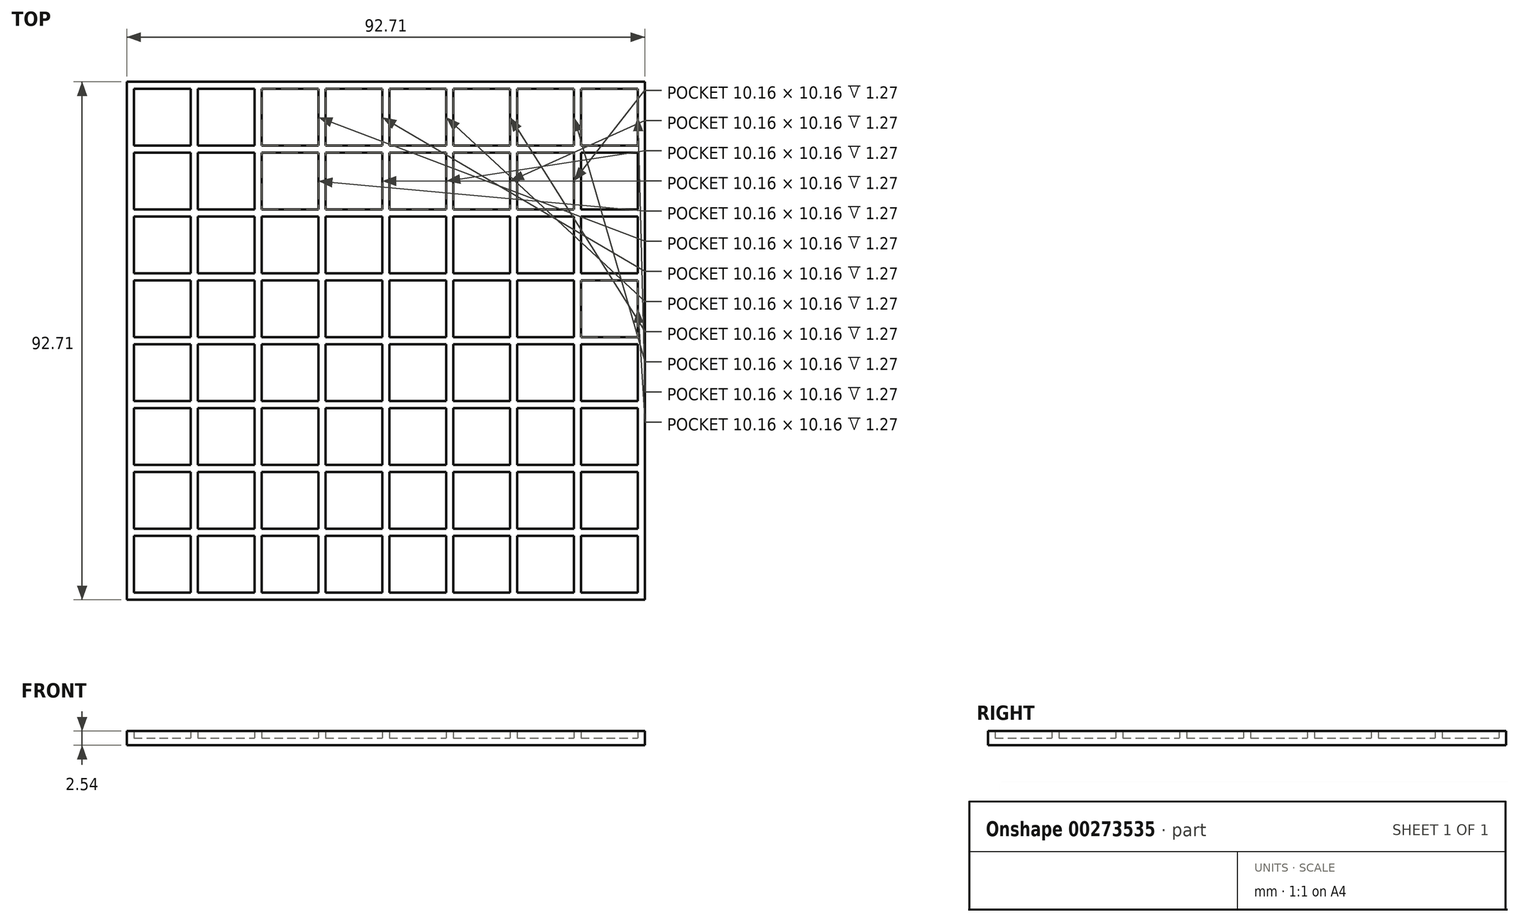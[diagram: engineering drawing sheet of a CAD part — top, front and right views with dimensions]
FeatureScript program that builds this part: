
annotation { "Feature Type Name" : "Feature", "Feature Type Description" : "" }
export const myFeature = defineFeature(function(context is Context, id is Id, definition is map)
    precondition{}
    {
        {
            var Q0;
            Q0=qCreatedBy(makeId("Top.planeOp"),FACE);
            var sketch = newSketch(context, id + "F0", { "sketchPlane" : qUnion([Q0])});
            skLineSegment(sketch, "E0.top", {"start": v(0, 92.7) * mm, "end": v(92.7, 92.7) * mm});
            skLineSegment(sketch, "E0.left", {"start": v(0, 0) * mm, "end": v(0, 92.7) * mm});
            skLineSegment(sketch, "E0.right", {"start": v(92.7, 0) * mm, "end": v(92.7, 92.7) * mm});
            skLineSegment(sketch, "E1.bottom", {"start": v(1.27, 1.27) * mm, "end": v(11.43, 1.27) * mm});
            skLineSegment(sketch, "E1.top", {"start": v(1.27, 11.43) * mm, "end": v(11.43, 11.43) * mm});
            skLineSegment(sketch, "E1.left", {"start": v(1.27, 1.27) * mm, "end": v(1.27, 11.43) * mm});
            skLineSegment(sketch, "E1.right", {"start": v(11.43, 1.27) * mm, "end": v(11.43, 11.43) * mm});
            skLineSegment(sketch, "E2.bottom", {"start": v(12.7, 1.27) * mm, "end": v(22.86, 1.27) * mm});
            skLineSegment(sketch, "E2.top", {"start": v(12.7, 11.43) * mm, "end": v(22.86, 11.43) * mm});
            skLineSegment(sketch, "E2.left", {"start": v(12.7, 1.27) * mm, "end": v(12.7, 11.43) * mm});
            skLineSegment(sketch, "E2.right", {"start": v(22.86, 1.27) * mm, "end": v(22.86, 11.43) * mm});
            skLineSegment(sketch, "E3.bottom", {"start": v(24.13, 1.27) * mm, "end": v(34.3, 1.27) * mm});
            skLineSegment(sketch, "E3.top", {"start": v(24.13, 11.43) * mm, "end": v(34.3, 11.43) * mm});
            skLineSegment(sketch, "E3.left", {"start": v(24.13, 1.27) * mm, "end": v(24.13, 11.43) * mm});
            skLineSegment(sketch, "E3.right", {"start": v(34.3, 1.27) * mm, "end": v(34.3, 11.43) * mm});
            skLineSegment(sketch, "E4.bottom", {"start": v(35.56, 1.27) * mm, "end": v(45.72, 1.27) * mm});
            skLineSegment(sketch, "E4.top", {"start": v(35.56, 11.43) * mm, "end": v(45.72, 11.43) * mm});
            skLineSegment(sketch, "E4.left", {"start": v(35.56, 1.27) * mm, "end": v(35.56, 11.43) * mm});
            skLineSegment(sketch, "E4.right", {"start": v(45.72, 1.27) * mm, "end": v(45.72, 11.43) * mm});
            skLineSegment(sketch, "E5.bottom", {"start": v(47, 1.27) * mm, "end": v(57.15, 1.27) * mm});
            skLineSegment(sketch, "E5.top", {"start": v(47, 11.43) * mm, "end": v(57.15, 11.43) * mm});
            skLineSegment(sketch, "E5.left", {"start": v(47, 1.27) * mm, "end": v(47, 11.43) * mm});
            skLineSegment(sketch, "E5.right", {"start": v(57.15, 1.27) * mm, "end": v(57.15, 11.43) * mm});
            skLineSegment(sketch, "E6.bottom", {"start": v(58.42, 1.27) * mm, "end": v(68.58, 1.27) * mm});
            skLineSegment(sketch, "E6.top", {"start": v(58.42, 11.43) * mm, "end": v(68.58, 11.43) * mm});
            skLineSegment(sketch, "E6.left", {"start": v(58.42, 1.27) * mm, "end": v(58.42, 11.43) * mm});
            skLineSegment(sketch, "E6.right", {"start": v(68.58, 1.27) * mm, "end": v(68.58, 11.43) * mm});
            skLineSegment(sketch, "E7.bottom", {"start": v(69.85, 1.27) * mm, "end": v(80.01, 1.27) * mm});
            skLineSegment(sketch, "E7.top", {"start": v(69.85, 11.43) * mm, "end": v(80.01, 11.43) * mm});
            skLineSegment(sketch, "E7.left", {"start": v(69.85, 1.27) * mm, "end": v(69.85, 11.43) * mm});
            skLineSegment(sketch, "E7.right", {"start": v(80.01, 1.27) * mm, "end": v(80.01, 11.43) * mm});
            skLineSegment(sketch, "E8.bottom", {"start": v(81.28, 1.27) * mm, "end": v(91.44, 1.27) * mm});
            skLineSegment(sketch, "E8.top", {"start": v(81.28, 11.43) * mm, "end": v(91.44, 11.43) * mm});
            skLineSegment(sketch, "E8.left", {"start": v(81.28, 1.27) * mm, "end": v(81.28, 11.43) * mm});
            skLineSegment(sketch, "E8.right", {"start": v(91.44, 1.27) * mm, "end": v(91.44, 11.43) * mm});
            skLineSegment(sketch, "E9", {"start": v(0, 0) * mm, "end": v(92.7, 0) * mm});
            skLineSegment(sketch, "E10.bottom", {"start": v(1.27, 12.7) * mm, "end": v(11.43, 12.7) * mm});
            skLineSegment(sketch, "E10.top", {"start": v(1.27, 22.86) * mm, "end": v(11.43, 22.86) * mm});
            skLineSegment(sketch, "E10.left", {"start": v(1.27, 12.7) * mm, "end": v(1.27, 22.86) * mm});
            skLineSegment(sketch, "E10.right", {"start": v(11.43, 12.7) * mm, "end": v(11.43, 22.86) * mm});
            skLineSegment(sketch, "E11.bottom", {"start": v(1.27, 24.13) * mm, "end": v(11.43, 24.13) * mm});
            skLineSegment(sketch, "E11.top", {"start": v(1.27, 34.3) * mm, "end": v(11.43, 34.3) * mm});
            skLineSegment(sketch, "E11.left", {"start": v(1.27, 24.13) * mm, "end": v(1.27, 34.3) * mm});
            skLineSegment(sketch, "E11.right", {"start": v(11.43, 24.13) * mm, "end": v(11.43, 34.3) * mm});
            skLineSegment(sketch, "E12.bottom", {"start": v(1.27, 35.56) * mm, "end": v(11.43, 35.56) * mm});
            skLineSegment(sketch, "E12.top", {"start": v(1.27, 45.72) * mm, "end": v(11.43, 45.72) * mm});
            skLineSegment(sketch, "E12.left", {"start": v(1.27, 35.56) * mm, "end": v(1.27, 45.72) * mm});
            skLineSegment(sketch, "E12.right", {"start": v(11.43, 35.56) * mm, "end": v(11.43, 45.72) * mm});
            skLineSegment(sketch, "E13.bottom", {"start": v(12.7, 12.7) * mm, "end": v(22.86, 12.7) * mm});
            skLineSegment(sketch, "E13.top", {"start": v(12.7, 22.86) * mm, "end": v(22.86, 22.86) * mm});
            skLineSegment(sketch, "E13.left", {"start": v(12.7, 12.7) * mm, "end": v(12.7, 22.86) * mm});
            skLineSegment(sketch, "E13.right", {"start": v(22.86, 12.7) * mm, "end": v(22.86, 22.86) * mm});
            skLineSegment(sketch, "E14.bottom", {"start": v(24.13, 12.7) * mm, "end": v(34.3, 12.7) * mm});
            skLineSegment(sketch, "E14.top", {"start": v(24.13, 22.86) * mm, "end": v(34.3, 22.86) * mm});
            skLineSegment(sketch, "E14.left", {"start": v(24.13, 12.7) * mm, "end": v(24.13, 22.86) * mm});
            skLineSegment(sketch, "E14.right", {"start": v(34.3, 12.7) * mm, "end": v(34.3, 22.86) * mm});
            skLineSegment(sketch, "E15.bottom", {"start": v(35.56, 12.7) * mm, "end": v(45.72, 12.7) * mm});
            skLineSegment(sketch, "E15.top", {"start": v(35.56, 22.86) * mm, "end": v(45.72, 22.86) * mm});
            skLineSegment(sketch, "E15.left", {"start": v(35.56, 12.7) * mm, "end": v(35.56, 22.86) * mm});
            skLineSegment(sketch, "E15.right", {"start": v(45.72, 12.7) * mm, "end": v(45.72, 22.86) * mm});
            skLineSegment(sketch, "E16.bottom", {"start": v(47, 12.7) * mm, "end": v(57.15, 12.7) * mm});
            skLineSegment(sketch, "E16.top", {"start": v(47, 22.86) * mm, "end": v(57.15, 22.86) * mm});
            skLineSegment(sketch, "E16.left", {"start": v(47, 12.7) * mm, "end": v(47, 22.86) * mm});
            skLineSegment(sketch, "E16.right", {"start": v(57.15, 12.7) * mm, "end": v(57.15, 22.86) * mm});
            skLineSegment(sketch, "E17.bottom", {"start": v(58.42, 12.7) * mm, "end": v(68.58, 12.7) * mm});
            skLineSegment(sketch, "E17.top", {"start": v(58.42, 22.86) * mm, "end": v(68.58, 22.86) * mm});
            skLineSegment(sketch, "E17.left", {"start": v(58.42, 12.7) * mm, "end": v(58.42, 22.86) * mm});
            skLineSegment(sketch, "E17.right", {"start": v(68.58, 12.7) * mm, "end": v(68.58, 22.86) * mm});
            skLineSegment(sketch, "E18.bottom", {"start": v(69.85, 12.7) * mm, "end": v(80.01, 12.7) * mm});
            skLineSegment(sketch, "E18.top", {"start": v(69.85, 22.86) * mm, "end": v(80.01, 22.86) * mm});
            skLineSegment(sketch, "E18.left", {"start": v(69.85, 12.7) * mm, "end": v(69.85, 22.86) * mm});
            skLineSegment(sketch, "E18.right", {"start": v(80.01, 12.7) * mm, "end": v(80.01, 22.86) * mm});
            skLineSegment(sketch, "E19.bottom", {"start": v(81.28, 12.7) * mm, "end": v(91.44, 12.7) * mm});
            skLineSegment(sketch, "E19.top", {"start": v(81.28, 22.86) * mm, "end": v(91.44, 22.86) * mm});
            skLineSegment(sketch, "E19.left", {"start": v(81.28, 12.7) * mm, "end": v(81.28, 22.86) * mm});
            skLineSegment(sketch, "E19.right", {"start": v(91.44, 12.7) * mm, "end": v(91.44, 22.86) * mm});
            skLineSegment(sketch, "E20.bottom", {"start": v(12.7, 24.13) * mm, "end": v(22.86, 24.13) * mm});
            skLineSegment(sketch, "E20.top", {"start": v(12.7, 34.3) * mm, "end": v(22.86, 34.3) * mm});
            skLineSegment(sketch, "E20.left", {"start": v(12.7, 24.13) * mm, "end": v(12.7, 34.3) * mm});
            skLineSegment(sketch, "E20.right", {"start": v(22.86, 24.13) * mm, "end": v(22.86, 34.3) * mm});
            skLineSegment(sketch, "E21.bottom", {"start": v(24.13, 24.13) * mm, "end": v(34.3, 24.13) * mm});
            skLineSegment(sketch, "E21.top", {"start": v(24.13, 34.3) * mm, "end": v(34.3, 34.3) * mm});
            skLineSegment(sketch, "E21.left", {"start": v(24.13, 24.13) * mm, "end": v(24.13, 34.3) * mm});
            skLineSegment(sketch, "E21.right", {"start": v(34.3, 24.13) * mm, "end": v(34.3, 34.3) * mm});
            skLineSegment(sketch, "E22.bottom", {"start": v(35.56, 24.13) * mm, "end": v(45.72, 24.13) * mm});
            skLineSegment(sketch, "E22.top", {"start": v(35.56, 34.3) * mm, "end": v(45.72, 34.3) * mm});
            skLineSegment(sketch, "E22.left", {"start": v(35.56, 24.13) * mm, "end": v(35.56, 34.3) * mm});
            skLineSegment(sketch, "E22.right", {"start": v(45.72, 24.13) * mm, "end": v(45.72, 34.3) * mm});
            skLineSegment(sketch, "E23.bottom", {"start": v(47, 24.13) * mm, "end": v(57.15, 24.13) * mm});
            skLineSegment(sketch, "E23.top", {"start": v(47, 34.3) * mm, "end": v(57.15, 34.3) * mm});
            skLineSegment(sketch, "E23.left", {"start": v(47, 24.13) * mm, "end": v(47, 34.3) * mm});
            skLineSegment(sketch, "E23.right", {"start": v(57.15, 24.13) * mm, "end": v(57.15, 34.3) * mm});
            skLineSegment(sketch, "E24.bottom", {"start": v(58.42, 24.13) * mm, "end": v(68.58, 24.13) * mm});
            skLineSegment(sketch, "E24.top", {"start": v(58.42, 34.3) * mm, "end": v(68.58, 34.3) * mm});
            skLineSegment(sketch, "E24.left", {"start": v(58.42, 24.13) * mm, "end": v(58.42, 34.3) * mm});
            skLineSegment(sketch, "E24.right", {"start": v(68.58, 24.13) * mm, "end": v(68.58, 34.3) * mm});
            skLineSegment(sketch, "E25.bottom", {"start": v(69.85, 24.13) * mm, "end": v(80.01, 24.13) * mm});
            skLineSegment(sketch, "E25.top", {"start": v(69.85, 34.3) * mm, "end": v(80.01, 34.3) * mm});
            skLineSegment(sketch, "E25.left", {"start": v(69.85, 24.13) * mm, "end": v(69.85, 34.3) * mm});
            skLineSegment(sketch, "E25.right", {"start": v(80.01, 24.13) * mm, "end": v(80.01, 34.3) * mm});
            skLineSegment(sketch, "E26.bottom", {"start": v(81.28, 24.13) * mm, "end": v(91.44, 24.13) * mm});
            skLineSegment(sketch, "E26.top", {"start": v(81.28, 34.3) * mm, "end": v(91.44, 34.3) * mm});
            skLineSegment(sketch, "E26.left", {"start": v(81.28, 24.13) * mm, "end": v(81.28, 34.3) * mm});
            skLineSegment(sketch, "E26.right", {"start": v(91.44, 24.13) * mm, "end": v(91.44, 34.3) * mm});
            skLineSegment(sketch, "E27.bottom", {"start": v(12.7, 35.56) * mm, "end": v(22.86, 35.56) * mm});
            skLineSegment(sketch, "E27.top", {"start": v(12.7, 45.72) * mm, "end": v(22.86, 45.72) * mm});
            skLineSegment(sketch, "E27.left", {"start": v(12.7, 35.56) * mm, "end": v(12.7, 45.72) * mm});
            skLineSegment(sketch, "E27.right", {"start": v(22.86, 35.56) * mm, "end": v(22.86, 45.72) * mm});
            skLineSegment(sketch, "E28.bottom", {"start": v(24.13, 35.56) * mm, "end": v(34.3, 35.56) * mm});
            skLineSegment(sketch, "E28.top", {"start": v(24.13, 45.72) * mm, "end": v(34.3, 45.72) * mm});
            skLineSegment(sketch, "E28.left", {"start": v(24.13, 35.56) * mm, "end": v(24.13, 45.72) * mm});
            skLineSegment(sketch, "E28.right", {"start": v(34.3, 35.56) * mm, "end": v(34.3, 45.72) * mm});
            skLineSegment(sketch, "E29.bottom", {"start": v(35.56, 35.56) * mm, "end": v(45.72, 35.56) * mm});
            skLineSegment(sketch, "E29.top", {"start": v(35.56, 45.72) * mm, "end": v(45.72, 45.72) * mm});
            skLineSegment(sketch, "E29.left", {"start": v(35.56, 35.56) * mm, "end": v(35.56, 45.72) * mm});
            skLineSegment(sketch, "E29.right", {"start": v(45.72, 35.56) * mm, "end": v(45.72, 45.72) * mm});
            skLineSegment(sketch, "E30.bottom", {"start": v(47, 35.56) * mm, "end": v(57.15, 35.56) * mm});
            skLineSegment(sketch, "E30.top", {"start": v(47, 45.72) * mm, "end": v(57.15, 45.72) * mm});
            skLineSegment(sketch, "E30.left", {"start": v(47, 35.56) * mm, "end": v(47, 45.72) * mm});
            skLineSegment(sketch, "E30.right", {"start": v(57.15, 35.56) * mm, "end": v(57.15, 45.72) * mm});
            skLineSegment(sketch, "E31.bottom", {"start": v(58.42, 35.56) * mm, "end": v(68.58, 35.56) * mm});
            skLineSegment(sketch, "E31.top", {"start": v(58.42, 45.72) * mm, "end": v(68.58, 45.72) * mm});
            skLineSegment(sketch, "E31.left", {"start": v(58.42, 35.56) * mm, "end": v(58.42, 45.72) * mm});
            skLineSegment(sketch, "E31.right", {"start": v(68.58, 35.56) * mm, "end": v(68.58, 45.72) * mm});
            skLineSegment(sketch, "E32.bottom", {"start": v(69.85, 35.56) * mm, "end": v(80.01, 35.56) * mm});
            skLineSegment(sketch, "E32.top", {"start": v(69.85, 45.72) * mm, "end": v(80.01, 45.72) * mm});
            skLineSegment(sketch, "E32.left", {"start": v(69.85, 35.56) * mm, "end": v(69.85, 45.72) * mm});
            skLineSegment(sketch, "E32.right", {"start": v(80.01, 35.56) * mm, "end": v(80.01, 45.72) * mm});
            skLineSegment(sketch, "E33.bottom", {"start": v(81.28, 35.56) * mm, "end": v(91.44, 35.56) * mm});
            skLineSegment(sketch, "E33.top", {"start": v(81.28, 45.72) * mm, "end": v(91.44, 45.72) * mm});
            skLineSegment(sketch, "E33.left", {"start": v(81.28, 35.56) * mm, "end": v(81.28, 45.72) * mm});
            skLineSegment(sketch, "E33.right", {"start": v(91.44, 35.56) * mm, "end": v(91.44, 45.72) * mm});
            skLineSegment(sketch, "E34.bottom", {"start": v(1.27, 47) * mm, "end": v(11.43, 47) * mm});
            skLineSegment(sketch, "E34.top", {"start": v(1.27, 57.15) * mm, "end": v(11.43, 57.15) * mm});
            skLineSegment(sketch, "E34.left", {"start": v(1.27, 47) * mm, "end": v(1.27, 57.15) * mm});
            skLineSegment(sketch, "E34.right", {"start": v(11.43, 47) * mm, "end": v(11.43, 57.15) * mm});
            skLineSegment(sketch, "E35.bottom", {"start": v(12.7, 47) * mm, "end": v(22.86, 47) * mm});
            skLineSegment(sketch, "E35.top", {"start": v(12.7, 57.15) * mm, "end": v(22.86, 57.15) * mm});
            skLineSegment(sketch, "E35.left", {"start": v(12.7, 47) * mm, "end": v(12.7, 57.15) * mm});
            skLineSegment(sketch, "E35.right", {"start": v(22.86, 47) * mm, "end": v(22.86, 57.15) * mm});
            skLineSegment(sketch, "E36.bottom", {"start": v(24.13, 47) * mm, "end": v(34.3, 47) * mm});
            skLineSegment(sketch, "E36.top", {"start": v(24.13, 57.15) * mm, "end": v(34.3, 57.15) * mm});
            skLineSegment(sketch, "E36.left", {"start": v(24.13, 47) * mm, "end": v(24.13, 57.15) * mm});
            skLineSegment(sketch, "E36.right", {"start": v(34.3, 47) * mm, "end": v(34.3, 57.15) * mm});
            skLineSegment(sketch, "E37.bottom", {"start": v(35.56, 47) * mm, "end": v(45.72, 47) * mm});
            skLineSegment(sketch, "E37.top", {"start": v(35.56, 57.15) * mm, "end": v(45.72, 57.15) * mm});
            skLineSegment(sketch, "E37.left", {"start": v(35.56, 47) * mm, "end": v(35.56, 57.15) * mm});
            skLineSegment(sketch, "E37.right", {"start": v(45.72, 47) * mm, "end": v(45.72, 57.15) * mm});
            skLineSegment(sketch, "E38.bottom", {"start": v(47, 47) * mm, "end": v(57.15, 47) * mm});
            skLineSegment(sketch, "E38.top", {"start": v(47, 57.15) * mm, "end": v(57.15, 57.15) * mm});
            skLineSegment(sketch, "E38.left", {"start": v(47, 47) * mm, "end": v(47, 57.15) * mm});
            skLineSegment(sketch, "E38.right", {"start": v(57.15, 47) * mm, "end": v(57.15, 57.15) * mm});
            skLineSegment(sketch, "E39.bottom", {"start": v(58.42, 47) * mm, "end": v(68.58, 47) * mm});
            skLineSegment(sketch, "E39.top", {"start": v(58.42, 57.15) * mm, "end": v(68.58, 57.15) * mm});
            skLineSegment(sketch, "E39.left", {"start": v(58.42, 47) * mm, "end": v(58.42, 57.15) * mm});
            skLineSegment(sketch, "E39.right", {"start": v(68.58, 47) * mm, "end": v(68.58, 57.15) * mm});
            skLineSegment(sketch, "E40.bottom", {"start": v(69.85, 47) * mm, "end": v(80.01, 47) * mm});
            skLineSegment(sketch, "E40.top", {"start": v(69.85, 57.15) * mm, "end": v(80.01, 57.15) * mm});
            skLineSegment(sketch, "E40.left", {"start": v(69.85, 47) * mm, "end": v(69.85, 57.15) * mm});
            skLineSegment(sketch, "E40.right", {"start": v(80.01, 47) * mm, "end": v(80.01, 57.15) * mm});
            skLineSegment(sketch, "E41.bottom", {"start": v(81.28, 47) * mm, "end": v(81.28, 47) * mm});
            skLineSegment(sketch, "E41.top", {"start": v(81.28, 57.15) * mm, "end": v(81.28, 57.15) * mm});
            skLineSegment(sketch, "E42.bottom", {"start": v(1.27, 58.42) * mm, "end": v(11.43, 58.42) * mm});
            skLineSegment(sketch, "E42.top", {"start": v(1.27, 68.58) * mm, "end": v(11.43, 68.58) * mm});
            skLineSegment(sketch, "E42.left", {"start": v(1.27, 58.42) * mm, "end": v(1.27, 68.58) * mm});
            skLineSegment(sketch, "E42.right", {"start": v(11.43, 58.42) * mm, "end": v(11.43, 68.58) * mm});
            skLineSegment(sketch, "E43.bottom", {"start": v(1.27, 69.85) * mm, "end": v(11.43, 69.85) * mm});
            skLineSegment(sketch, "E43.top", {"start": v(1.27, 80.01) * mm, "end": v(11.43, 80.01) * mm});
            skLineSegment(sketch, "E43.left", {"start": v(1.27, 69.85) * mm, "end": v(1.27, 80.01) * mm});
            skLineSegment(sketch, "E43.right", {"start": v(11.43, 69.85) * mm, "end": v(11.43, 80.01) * mm});
            skLineSegment(sketch, "E44.bottom", {"start": v(1.27, 81.28) * mm, "end": v(11.43, 81.28) * mm});
            skLineSegment(sketch, "E44.top", {"start": v(1.27, 91.44) * mm, "end": v(11.43, 91.44) * mm});
            skLineSegment(sketch, "E44.left", {"start": v(1.27, 81.28) * mm, "end": v(1.27, 91.44) * mm});
            skLineSegment(sketch, "E44.right", {"start": v(11.43, 81.28) * mm, "end": v(11.43, 91.44) * mm});
            skLineSegment(sketch, "E45.bottom", {"start": v(12.7, 58.42) * mm, "end": v(22.86, 58.42) * mm});
            skLineSegment(sketch, "E45.top", {"start": v(12.7, 68.58) * mm, "end": v(22.86, 68.58) * mm});
            skLineSegment(sketch, "E45.left", {"start": v(12.7, 58.42) * mm, "end": v(12.7, 68.58) * mm});
            skLineSegment(sketch, "E45.right", {"start": v(22.86, 58.42) * mm, "end": v(22.86, 68.58) * mm});
            skLineSegment(sketch, "E46.bottom", {"start": v(12.7, 69.85) * mm, "end": v(22.86, 69.85) * mm});
            skLineSegment(sketch, "E46.top", {"start": v(12.7, 80.01) * mm, "end": v(22.86, 80.01) * mm});
            skLineSegment(sketch, "E46.left", {"start": v(12.7, 69.85) * mm, "end": v(12.7, 80.01) * mm});
            skLineSegment(sketch, "E46.right", {"start": v(22.86, 69.85) * mm, "end": v(22.86, 80.01) * mm});
            skLineSegment(sketch, "E47.bottom", {"start": v(12.7, 81.28) * mm, "end": v(22.86, 81.28) * mm});
            skLineSegment(sketch, "E47.top", {"start": v(12.7, 91.44) * mm, "end": v(22.86, 91.44) * mm});
            skLineSegment(sketch, "E47.left", {"start": v(12.7, 81.28) * mm, "end": v(12.7, 91.44) * mm});
            skLineSegment(sketch, "E47.right", {"start": v(22.86, 81.28) * mm, "end": v(22.86, 91.44) * mm});
            skLineSegment(sketch, "E48.bottom", {"start": v(24.13, 58.42) * mm, "end": v(34.3, 58.42) * mm});
            skLineSegment(sketch, "E48.top", {"start": v(24.13, 68.58) * mm, "end": v(34.3, 68.58) * mm});
            skLineSegment(sketch, "E48.left", {"start": v(24.13, 58.42) * mm, "end": v(24.13, 68.58) * mm});
            skLineSegment(sketch, "E48.right", {"start": v(34.29, 58.42) * mm, "end": v(34.29, 68.58) * mm});
            skLineSegment(sketch, "E49.bottom", {"start": v(35.56, 58.42) * mm, "end": v(45.72, 58.42) * mm});
            skLineSegment(sketch, "E49.top", {"start": v(35.56, 68.58) * mm, "end": v(45.72, 68.58) * mm});
            skLineSegment(sketch, "E49.left", {"start": v(35.56, 58.42) * mm, "end": v(35.56, 68.58) * mm});
            skLineSegment(sketch, "E49.right", {"start": v(45.72, 58.42) * mm, "end": v(45.72, 68.58) * mm});
            skLineSegment(sketch, "E50.bottom", {"start": v(47, 58.42) * mm, "end": v(57.15, 58.42) * mm});
            skLineSegment(sketch, "E50.top", {"start": v(47, 68.58) * mm, "end": v(57.15, 68.58) * mm});
            skLineSegment(sketch, "E50.left", {"start": v(47, 58.42) * mm, "end": v(47, 68.58) * mm});
            skLineSegment(sketch, "E50.right", {"start": v(57.15, 58.42) * mm, "end": v(57.15, 68.58) * mm});
            skLineSegment(sketch, "E51.bottom", {"start": v(58.42, 58.42) * mm, "end": v(68.58, 58.42) * mm});
            skLineSegment(sketch, "E51.top", {"start": v(58.42, 68.58) * mm, "end": v(68.58, 68.58) * mm});
            skLineSegment(sketch, "E51.left", {"start": v(58.42, 58.42) * mm, "end": v(58.42, 68.58) * mm});
            skLineSegment(sketch, "E51.right", {"start": v(68.58, 58.42) * mm, "end": v(68.58, 68.58) * mm});
            skLineSegment(sketch, "E52.bottom", {"start": v(69.85, 58.42) * mm, "end": v(80.01, 58.42) * mm});
            skLineSegment(sketch, "E52.top", {"start": v(69.85, 68.58) * mm, "end": v(80.01, 68.58) * mm});
            skLineSegment(sketch, "E52.left", {"start": v(69.85, 58.42) * mm, "end": v(69.85, 68.58) * mm});
            skLineSegment(sketch, "E52.right", {"start": v(80.01, 58.42) * mm, "end": v(80.01, 68.58) * mm});
            skLineSegment(sketch, "E53.bottom", {"start": v(81.28, 58.42) * mm, "end": v(91.44, 58.42) * mm});
            skLineSegment(sketch, "E53.top", {"start": v(81.28, 68.58) * mm, "end": v(91.44, 68.58) * mm});
            skLineSegment(sketch, "E53.left", {"start": v(81.28, 58.42) * mm, "end": v(81.28, 68.58) * mm});
            skLineSegment(sketch, "E53.right", {"start": v(91.44, 58.42) * mm, "end": v(91.44, 68.58) * mm});
            skLineSegment(sketch, "E54.bottom", {"start": v(81.28, 69.85) * mm, "end": v(91.44, 69.85) * mm});
            skLineSegment(sketch, "E54.top", {"start": v(81.28, 80.01) * mm, "end": v(91.44, 80.01) * mm});
            skLineSegment(sketch, "E54.left", {"start": v(81.28, 69.85) * mm, "end": v(81.28, 80.01) * mm});
            skLineSegment(sketch, "E54.right", {"start": v(91.44, 69.85) * mm, "end": v(91.44, 80.01) * mm});
            skLineSegment(sketch, "E55.bottom", {"start": v(69.85, 69.85) * mm, "end": v(80.01, 69.85) * mm});
            skLineSegment(sketch, "E55.top", {"start": v(69.85, 80.01) * mm, "end": v(80.01, 80.01) * mm});
            skLineSegment(sketch, "E55.left", {"start": v(69.85, 69.85) * mm, "end": v(69.85, 80.01) * mm});
            skLineSegment(sketch, "E55.right", {"start": v(80.01, 69.85) * mm, "end": v(80.01, 80.01) * mm});
            skLineSegment(sketch, "E56.bottom", {"start": v(58.42, 69.85) * mm, "end": v(68.58, 69.85) * mm});
            skLineSegment(sketch, "E56.top", {"start": v(58.42, 80.01) * mm, "end": v(68.58, 80.01) * mm});
            skLineSegment(sketch, "E56.left", {"start": v(58.42, 69.85) * mm, "end": v(58.42, 80.01) * mm});
            skLineSegment(sketch, "E56.right", {"start": v(68.58, 69.85) * mm, "end": v(68.58, 80.01) * mm});
            skLineSegment(sketch, "E57.bottom", {"start": v(47, 69.85) * mm, "end": v(57.15, 69.85) * mm});
            skLineSegment(sketch, "E57.top", {"start": v(46.99, 80.01) * mm, "end": v(57.15, 80.01) * mm});
            skLineSegment(sketch, "E57.left", {"start": v(46.99, 69.85) * mm, "end": v(46.99, 80.01) * mm});
            skLineSegment(sketch, "E57.right", {"start": v(57.15, 69.85) * mm, "end": v(57.15, 80.01) * mm});
            skLineSegment(sketch, "E58.bottom", {"start": v(35.56, 69.85) * mm, "end": v(45.72, 69.85) * mm});
            skLineSegment(sketch, "E58.top", {"start": v(35.56, 80.01) * mm, "end": v(45.72, 80.01) * mm});
            skLineSegment(sketch, "E58.left", {"start": v(35.56, 69.85) * mm, "end": v(35.56, 80.01) * mm});
            skLineSegment(sketch, "E58.right", {"start": v(45.72, 69.85) * mm, "end": v(45.72, 80.01) * mm});
            skLineSegment(sketch, "E59.bottom", {"start": v(24.13, 69.85) * mm, "end": v(34.3, 69.85) * mm});
            skLineSegment(sketch, "E59.top", {"start": v(24.13, 80.01) * mm, "end": v(34.3, 80.01) * mm});
            skLineSegment(sketch, "E59.left", {"start": v(24.13, 69.85) * mm, "end": v(24.13, 80.01) * mm});
            skLineSegment(sketch, "E59.right", {"start": v(34.3, 69.85) * mm, "end": v(34.3, 80.01) * mm});
            skLineSegment(sketch, "E60.bottom", {"start": v(24.13, 81.28) * mm, "end": v(34.29, 81.28) * mm});
            skLineSegment(sketch, "E60.top", {"start": v(24.13, 91.44) * mm, "end": v(34.29, 91.44) * mm});
            skLineSegment(sketch, "E60.left", {"start": v(24.13, 81.28) * mm, "end": v(24.13, 91.44) * mm});
            skLineSegment(sketch, "E60.right", {"start": v(34.29, 81.28) * mm, "end": v(34.29, 91.44) * mm});
            skLineSegment(sketch, "E61.bottom", {"start": v(35.56, 81.28) * mm, "end": v(45.72, 81.28) * mm});
            skLineSegment(sketch, "E61.top", {"start": v(35.56, 91.44) * mm, "end": v(45.72, 91.44) * mm});
            skLineSegment(sketch, "E61.left", {"start": v(35.56, 81.28) * mm, "end": v(35.56, 91.44) * mm});
            skLineSegment(sketch, "E61.right", {"start": v(45.72, 81.28) * mm, "end": v(45.72, 91.44) * mm});
            skLineSegment(sketch, "E62.bottom", {"start": v(47, 81.28) * mm, "end": v(57.15, 81.28) * mm});
            skLineSegment(sketch, "E62.top", {"start": v(47, 91.44) * mm, "end": v(57.15, 91.44) * mm});
            skLineSegment(sketch, "E62.left", {"start": v(47, 81.28) * mm, "end": v(47, 91.44) * mm});
            skLineSegment(sketch, "E62.right", {"start": v(57.15, 81.28) * mm, "end": v(57.15, 91.44) * mm});
            skLineSegment(sketch, "E63.bottom", {"start": v(58.42, 81.28) * mm, "end": v(68.58, 81.28) * mm});
            skLineSegment(sketch, "E63.top", {"start": v(58.42, 91.44) * mm, "end": v(68.58, 91.44) * mm});
            skLineSegment(sketch, "E63.left", {"start": v(58.42, 81.28) * mm, "end": v(58.42, 91.44) * mm});
            skLineSegment(sketch, "E63.right", {"start": v(68.58, 81.28) * mm, "end": v(68.58, 91.44) * mm});
            skLineSegment(sketch, "E64.bottom", {"start": v(69.85, 81.28) * mm, "end": v(80.01, 81.28) * mm});
            skLineSegment(sketch, "E64.top", {"start": v(69.85, 91.44) * mm, "end": v(80.01, 91.44) * mm});
            skLineSegment(sketch, "E64.left", {"start": v(69.85, 81.28) * mm, "end": v(69.85, 91.44) * mm});
            skLineSegment(sketch, "E64.right", {"start": v(80.01, 81.28) * mm, "end": v(80.01, 91.44) * mm});
            skLineSegment(sketch, "E65.bottom", {"start": v(81.28, 81.28) * mm, "end": v(91.44, 81.28) * mm});
            skLineSegment(sketch, "E65.top", {"start": v(81.28, 91.44) * mm, "end": v(91.44, 91.44) * mm});
            skLineSegment(sketch, "E65.left", {"start": v(81.28, 81.28) * mm, "end": v(81.28, 91.44) * mm});
            skLineSegment(sketch, "E65.right", {"start": v(91.44, 81.28) * mm, "end": v(91.44, 91.44) * mm});
            skLineSegment(sketch, "E66", {"start": v(24.13, 1.27) * mm, "end": v(24.13, 91.44) * mm, "construction": true});
            skLineSegment(sketch, "E67", {"start": v(35.56, 11.43) * mm, "end": v(35.56, 92.7) * mm, "construction": true});
            skLineSegment(sketch, "E68", {"start": v(34.3, 22.86) * mm, "end": v(92.7, 22.86) * mm, "construction": true});
            skLineSegment(sketch, "E69", {"start": v(34.3, 34.3) * mm, "end": v(92.7, 34.3) * mm, "construction": true});
            skLineSegment(sketch, "E70", {"start": v(34.3, 45.72) * mm, "end": v(92.7, 45.72) * mm, "construction": true});
            skLineSegment(sketch, "E71", {"start": v(47, 11.43) * mm, "end": v(47, 92.7) * mm, "construction": true});
            skLineSegment(sketch, "E72", {"start": v(34.3, 12.7) * mm, "end": v(92.7, 12.7) * mm, "construction": true});
            skLineSegment(sketch, "E73", {"start": v(34.3, 35.56) * mm, "end": v(92.7, 35.56) * mm, "construction": true});
            skLineSegment(sketch, "E74", {"start": v(34.3, 24.13) * mm, "end": v(92.7, 24.13) * mm, "construction": true});
            skLineSegment(sketch, "E75", {"start": v(45.72, 11.43) * mm, "end": v(45.72, 92.7) * mm, "construction": true});
            skLineSegment(sketch, "E76", {"start": v(34.3, 57.15) * mm, "end": v(92.7, 57.15) * mm, "construction": true});
            skLineSegment(sketch, "E77", {"start": v(34.3, 58.42) * mm, "end": v(92.7, 58.42) * mm, "construction": true});
            skLineSegment(sketch, "E78", {"start": v(34.3, 68.58) * mm, "end": v(92.7, 68.58) * mm, "construction": true});
            skLineSegment(sketch, "E79", {"start": v(34.3, 69.85) * mm, "end": v(92.7, 69.85) * mm, "construction": true});
            skLineSegment(sketch, "E80", {"start": v(34.3, 80.01) * mm, "end": v(92.7, 80.01) * mm, "construction": true});
            skLineSegment(sketch, "E81", {"start": v(34.29, 81.28) * mm, "end": v(92.7, 81.28) * mm, "construction": true});
            skLineSegment(sketch, "E82", {"start": v(34.29, 91.44) * mm, "end": v(92.7, 91.44) * mm, "construction": true});
            skPoint(sketch, "E82.endSnap0", {"position": v(40.64, 91.44) * mm});
            skLineSegment(sketch, "E83", {"start": v(34.3, 47) * mm, "end": v(92.7, 47) * mm, "construction": true});
            skLineSegment(sketch, "E84", {"start": v(57.15, 11.43) * mm, "end": v(57.15, 92.7) * mm, "construction": true});
            skLineSegment(sketch, "E85", {"start": v(58.42, 11.43) * mm, "end": v(58.42, 92.7) * mm, "construction": true});
            skLineSegment(sketch, "E86", {"start": v(68.58, 11.43) * mm, "end": v(68.58, 92.7) * mm, "construction": true});
            skLineSegment(sketch, "E87", {"start": v(69.85, 11.43) * mm, "end": v(69.85, 92.7) * mm, "construction": true});
            skLineSegment(sketch, "E88", {"start": v(80.01, 11.43) * mm, "end": v(80.01, 92.7) * mm, "construction": true});
            skPoint(sketch, "E88.endSnap0", {"position": v(80.01, 63.5) * mm});
            skLineSegment(sketch, "E89", {"start": v(91.44, 11.43) * mm, "end": v(91.44, 92.71) * mm, "construction": true});
            skLineSegment(sketch, "E90", {"start": v(81.28, 11.43) * mm, "end": v(81.28, 92.71) * mm, "construction": true});
            skLineSegment(sketch, "E91.bottom", {"start": v(81.28, 47) * mm, "end": v(91.44, 47) * mm});
            skLineSegment(sketch, "E91.top", {"start": v(81.28, 57.15) * mm, "end": v(91.44, 57.15) * mm});
            skLineSegment(sketch, "E91.left", {"start": v(81.28, 47) * mm, "end": v(81.28, 57.15) * mm});
            skLineSegment(sketch, "E91.right", {"start": v(91.44, 47) * mm, "end": v(91.44, 57.15) * mm});
            skSolve(sketch);
        }
        {
            var Q0;
            Q0=makeQuery(id+"F0.imprint","IMPRINT",FACE,{"disambiguationData":[TD([[makeQuery(id+"F0.imprint","IMPRINT",EDGE,{"derivedFrom":sQuery(id+"F0.wireOp",EDGE,"E0.top")}),-1.0]])]});
            extrude(context, id + "F1", {"entities" : qUnion([Q0]), "depth" : 2.54 * mm});
        }
        {
            var Q0;
            Q0=makeQuery(id+"F0.imprint","IMPRINT",FACE,{"disambiguationData":[TD([[makeQuery(id+"F0.imprint","IMPRINT",EDGE,{"derivedFrom":sQuery(id+"F0.wireOp",EDGE,"E44.bottom")}),1.0]])]});
            var Q1;
            Q1=makeQuery(id+"F0.imprint","IMPRINT",FACE,{"disambiguationData":[TD([[makeQuery(id+"F0.imprint","IMPRINT",EDGE,{"derivedFrom":sQuery(id+"F0.wireOp",EDGE,"E47.bottom")}),1.0]])]});
            var Q2;
            Q2=makeQuery(id+"F0.imprint","IMPRINT",FACE,{"disambiguationData":[TD([[makeQuery(id+"F0.imprint","IMPRINT",EDGE,{"derivedFrom":sQuery(id+"F0.wireOp",EDGE,"E46.bottom")}),1.0]])]});
            var Q3;
            Q3=makeQuery(id+"F0.imprint","IMPRINT",FACE,{"disambiguationData":[TD([[makeQuery(id+"F0.imprint","IMPRINT",EDGE,{"derivedFrom":sQuery(id+"F0.wireOp",EDGE,"E43.bottom")}),1.0]])]});
            var Q4;
            Q4=makeQuery(id+"F0.imprint","IMPRINT",FACE,{"disambiguationData":[TD([[makeQuery(id+"F0.imprint","IMPRINT",EDGE,{"derivedFrom":sQuery(id+"F0.wireOp",EDGE,"E42.bottom")}),1.0]])]});
            var Q5;
            Q5=makeQuery(id+"F0.imprint","IMPRINT",FACE,{"disambiguationData":[TD([[makeQuery(id+"F0.imprint","IMPRINT",EDGE,{"derivedFrom":sQuery(id+"F0.wireOp",EDGE,"E45.bottom")}),1.0]])]});
            var Q6;
            Q6=makeQuery(id+"F0.imprint","IMPRINT",FACE,{"disambiguationData":[TD([[makeQuery(id+"F0.imprint","IMPRINT",EDGE,{"derivedFrom":sQuery(id+"F0.wireOp",EDGE,"E34.bottom")}),1.0]])]});
            var Q7;
            Q7=makeQuery(id+"F0.imprint","IMPRINT",FACE,{"disambiguationData":[TD([[makeQuery(id+"F0.imprint","IMPRINT",EDGE,{"derivedFrom":sQuery(id+"F0.wireOp",EDGE,"E12.bottom")}),1.0]])]});
            var Q8;
            Q8=makeQuery(id+"F0.imprint","IMPRINT",FACE,{"disambiguationData":[TD([[makeQuery(id+"F0.imprint","IMPRINT",EDGE,{"derivedFrom":sQuery(id+"F0.wireOp",EDGE,"E11.bottom")}),1.0]])]});
            var Q9;
            Q9=makeQuery(id+"F0.imprint","IMPRINT",FACE,{"disambiguationData":[TD([[makeQuery(id+"F0.imprint","IMPRINT",EDGE,{"derivedFrom":sQuery(id+"F0.wireOp",EDGE,"E10.bottom")}),1.0]])]});
            var Q10;
            Q10=makeQuery(id+"F0.imprint","IMPRINT",FACE,{"disambiguationData":[TD([[makeQuery(id+"F0.imprint","IMPRINT",EDGE,{"derivedFrom":sQuery(id+"F0.wireOp",EDGE,"E1.bottom")}),1.0]])]});
            var Q11;
            Q11=makeQuery(id+"F0.imprint","IMPRINT",FACE,{"disambiguationData":[TD([[makeQuery(id+"F0.imprint","IMPRINT",EDGE,{"derivedFrom":sQuery(id+"F0.wireOp",EDGE,"E35.bottom")}),1.0]])]});
            var Q12;
            Q12=makeQuery(id+"F0.imprint","IMPRINT",FACE,{"disambiguationData":[TD([[makeQuery(id+"F0.imprint","IMPRINT",EDGE,{"derivedFrom":sQuery(id+"F0.wireOp",EDGE,"E27.bottom")}),1.0]])]});
            var Q13;
            Q13=makeQuery(id+"F0.imprint","IMPRINT",FACE,{"disambiguationData":[TD([[makeQuery(id+"F0.imprint","IMPRINT",EDGE,{"derivedFrom":sQuery(id+"F0.wireOp",EDGE,"E20.bottom")}),1.0]])]});
            var Q14;
            Q14=makeQuery(id+"F0.imprint","IMPRINT",FACE,{"disambiguationData":[TD([[makeQuery(id+"F0.imprint","IMPRINT",EDGE,{"derivedFrom":sQuery(id+"F0.wireOp",EDGE,"E13.bottom")}),1.0]])]});
            var Q15;
            Q15=makeQuery(id+"F0.imprint","IMPRINT",FACE,{"disambiguationData":[TD([[makeQuery(id+"F0.imprint","IMPRINT",EDGE,{"derivedFrom":sQuery(id+"F0.wireOp",EDGE,"E2.bottom")}),1.0]])]});
            var Q16;
            Q16=makeQuery(id+"F0.imprint","IMPRINT",FACE,{"disambiguationData":[TD([[makeQuery(id+"F0.imprint","IMPRINT",EDGE,{"derivedFrom":sQuery(id+"F0.wireOp",EDGE,"E3.bottom")}),1.0]])]});
            var Q17;
            Q17=makeQuery(id+"F0.imprint","IMPRINT",FACE,{"disambiguationData":[TD([[makeQuery(id+"F0.imprint","IMPRINT",EDGE,{"derivedFrom":sQuery(id+"F0.wireOp",EDGE,"E14.bottom")}),1.0]])]});
            var Q18;
            Q18=makeQuery(id+"F0.imprint","IMPRINT",FACE,{"disambiguationData":[TD([[makeQuery(id+"F0.imprint","IMPRINT",EDGE,{"derivedFrom":sQuery(id+"F0.wireOp",EDGE,"E21.bottom")}),1.0]])]});
            var Q19;
            Q19=makeQuery(id+"F0.imprint","IMPRINT",FACE,{"disambiguationData":[TD([[makeQuery(id+"F0.imprint","IMPRINT",EDGE,{"derivedFrom":sQuery(id+"F0.wireOp",EDGE,"E28.bottom")}),1.0]])]});
            var Q20;
            Q20=makeQuery(id+"F0.imprint","IMPRINT",FACE,{"disambiguationData":[TD([[makeQuery(id+"F0.imprint","IMPRINT",EDGE,{"derivedFrom":sQuery(id+"F0.wireOp",EDGE,"E36.bottom")}),1.0]])]});
            var Q21;
            Q21=makeQuery(id+"F0.imprint","IMPRINT",FACE,{"disambiguationData":[TD([[makeQuery(id+"F0.imprint","IMPRINT",EDGE,{"derivedFrom":sQuery(id+"F0.wireOp",EDGE,"E48.bottom")}),1.0]])]});
            var Q22;
            Q22=makeQuery(id+"F0.imprint","IMPRINT",FACE,{"disambiguationData":[TD([[makeQuery(id+"F0.imprint","IMPRINT",EDGE,{"derivedFrom":sQuery(id+"F0.wireOp",EDGE,"E59.bottom")}),1.0]])]});
            var Q23;
            Q23=makeQuery(id+"F0.imprint","IMPRINT",FACE,{"disambiguationData":[TD([[makeQuery(id+"F0.imprint","IMPRINT",EDGE,{"derivedFrom":sQuery(id+"F0.wireOp",EDGE,"E60.bottom")}),1.0]])]});
            var Q24;
            Q24=makeQuery(id+"F0.imprint","IMPRINT",FACE,{"disambiguationData":[TD([[makeQuery(id+"F0.imprint","IMPRINT",EDGE,{"derivedFrom":sQuery(id+"F0.wireOp",EDGE,"E61.bottom")}),1.0]])]});
            var Q25;
            Q25=makeQuery(id+"F0.imprint","IMPRINT",FACE,{"disambiguationData":[TD([[makeQuery(id+"F0.imprint","IMPRINT",EDGE,{"derivedFrom":sQuery(id+"F0.wireOp",EDGE,"E58.bottom")}),1.0]])]});
            var Q26;
            Q26=makeQuery(id+"F0.imprint","IMPRINT",FACE,{"disambiguationData":[TD([[makeQuery(id+"F0.imprint","IMPRINT",EDGE,{"derivedFrom":sQuery(id+"F0.wireOp",EDGE,"E49.bottom")}),1.0]])]});
            var Q27;
            Q27=makeQuery(id+"F0.imprint","IMPRINT",FACE,{"disambiguationData":[TD([[makeQuery(id+"F0.imprint","IMPRINT",EDGE,{"derivedFrom":sQuery(id+"F0.wireOp",EDGE,"E37.bottom")}),1.0]])]});
            var Q28;
            Q28=makeQuery(id+"F0.imprint","IMPRINT",FACE,{"disambiguationData":[TD([[makeQuery(id+"F0.imprint","IMPRINT",EDGE,{"derivedFrom":sQuery(id+"F0.wireOp",EDGE,"E29.bottom")}),1.0]])]});
            var Q29;
            Q29=makeQuery(id+"F0.imprint","IMPRINT",FACE,{"disambiguationData":[TD([[makeQuery(id+"F0.imprint","IMPRINT",EDGE,{"derivedFrom":sQuery(id+"F0.wireOp",EDGE,"E22.bottom")}),1.0]])]});
            var Q30;
            Q30=makeQuery(id+"F0.imprint","IMPRINT",FACE,{"disambiguationData":[TD([[makeQuery(id+"F0.imprint","IMPRINT",EDGE,{"derivedFrom":sQuery(id+"F0.wireOp",EDGE,"E15.bottom")}),1.0]])]});
            var Q31;
            Q31=makeQuery(id+"F0.imprint","IMPRINT",FACE,{"disambiguationData":[TD([[makeQuery(id+"F0.imprint","IMPRINT",EDGE,{"derivedFrom":sQuery(id+"F0.wireOp",EDGE,"E4.bottom")}),1.0]])]});
            var Q32;
            Q32=makeQuery(id+"F0.imprint","IMPRINT",FACE,{"disambiguationData":[TD([[makeQuery(id+"F0.imprint","IMPRINT",EDGE,{"derivedFrom":sQuery(id+"F0.wireOp",EDGE,"E5.bottom")}),1.0]])]});
            var Q33;
            Q33=makeQuery(id+"F0.imprint","IMPRINT",FACE,{"disambiguationData":[TD([[makeQuery(id+"F0.imprint","IMPRINT",EDGE,{"derivedFrom":sQuery(id+"F0.wireOp",EDGE,"E16.bottom")}),1.0]])]});
            var Q34;
            Q34=makeQuery(id+"F0.imprint","IMPRINT",FACE,{"disambiguationData":[TD([[makeQuery(id+"F0.imprint","IMPRINT",EDGE,{"derivedFrom":sQuery(id+"F0.wireOp",EDGE,"E23.bottom")}),1.0]])]});
            var Q35;
            Q35=makeQuery(id+"F0.imprint","IMPRINT",FACE,{"disambiguationData":[TD([[makeQuery(id+"F0.imprint","IMPRINT",EDGE,{"derivedFrom":sQuery(id+"F0.wireOp",EDGE,"E30.bottom")}),1.0]])]});
            var Q36;
            Q36=makeQuery(id+"F0.imprint","IMPRINT",FACE,{"disambiguationData":[TD([[makeQuery(id+"F0.imprint","IMPRINT",EDGE,{"derivedFrom":sQuery(id+"F0.wireOp",EDGE,"E38.bottom")}),1.0]])]});
            var Q37;
            Q37=makeQuery(id+"F0.imprint","IMPRINT",FACE,{"disambiguationData":[TD([[makeQuery(id+"F0.imprint","IMPRINT",EDGE,{"derivedFrom":sQuery(id+"F0.wireOp",EDGE,"E50.bottom")}),1.0]])]});
            var Q38;
            Q38=makeQuery(id+"F0.imprint","IMPRINT",FACE,{"disambiguationData":[TD([[makeQuery(id+"F0.imprint","IMPRINT",EDGE,{"derivedFrom":sQuery(id+"F0.wireOp",EDGE,"E57.bottom")}),1.0]])]});
            var Q39;
            Q39=makeQuery(id+"F0.imprint","IMPRINT",FACE,{"disambiguationData":[TD([[makeQuery(id+"F0.imprint","IMPRINT",EDGE,{"derivedFrom":sQuery(id+"F0.wireOp",EDGE,"E62.bottom")}),1.0]])]});
            var Q40;
            Q40=makeQuery(id+"F0.imprint","IMPRINT",FACE,{"disambiguationData":[TD([[makeQuery(id+"F0.imprint","IMPRINT",EDGE,{"derivedFrom":sQuery(id+"F0.wireOp",EDGE,"E63.bottom")}),1.0]])]});
            var Q41;
            Q41=makeQuery(id+"F0.imprint","IMPRINT",FACE,{"disambiguationData":[TD([[makeQuery(id+"F0.imprint","IMPRINT",EDGE,{"derivedFrom":sQuery(id+"F0.wireOp",EDGE,"E56.bottom")}),1.0]])]});
            var Q42;
            Q42=makeQuery(id+"F0.imprint","IMPRINT",FACE,{"disambiguationData":[TD([[makeQuery(id+"F0.imprint","IMPRINT",EDGE,{"derivedFrom":sQuery(id+"F0.wireOp",EDGE,"E51.bottom")}),1.0]])]});
            var Q43;
            Q43=makeQuery(id+"F0.imprint","IMPRINT",FACE,{"disambiguationData":[TD([[makeQuery(id+"F0.imprint","IMPRINT",EDGE,{"derivedFrom":sQuery(id+"F0.wireOp",EDGE,"E39.bottom")}),1.0]])]});
            var Q44;
            Q44=makeQuery(id+"F0.imprint","IMPRINT",FACE,{"disambiguationData":[TD([[makeQuery(id+"F0.imprint","IMPRINT",EDGE,{"derivedFrom":sQuery(id+"F0.wireOp",EDGE,"E31.bottom")}),1.0]])]});
            var Q45;
            Q45=makeQuery(id+"F0.imprint","IMPRINT",FACE,{"disambiguationData":[TD([[makeQuery(id+"F0.imprint","IMPRINT",EDGE,{"derivedFrom":sQuery(id+"F0.wireOp",EDGE,"E24.bottom")}),1.0]])]});
            var Q46;
            Q46=makeQuery(id+"F0.imprint","IMPRINT",FACE,{"disambiguationData":[TD([[makeQuery(id+"F0.imprint","IMPRINT",EDGE,{"derivedFrom":sQuery(id+"F0.wireOp",EDGE,"E17.bottom")}),1.0]])]});
            var Q47;
            Q47=makeQuery(id+"F0.imprint","IMPRINT",FACE,{"disambiguationData":[TD([[makeQuery(id+"F0.imprint","IMPRINT",EDGE,{"derivedFrom":sQuery(id+"F0.wireOp",EDGE,"E6.bottom")}),1.0]])]});
            var Q48;
            Q48=makeQuery(id+"F0.imprint","IMPRINT",FACE,{"disambiguationData":[TD([[makeQuery(id+"F0.imprint","IMPRINT",EDGE,{"derivedFrom":sQuery(id+"F0.wireOp",EDGE,"E7.bottom")}),1.0]])]});
            var Q49;
            Q49=makeQuery(id+"F0.imprint","IMPRINT",FACE,{"disambiguationData":[TD([[makeQuery(id+"F0.imprint","IMPRINT",EDGE,{"derivedFrom":sQuery(id+"F0.wireOp",EDGE,"E18.bottom")}),1.0]])]});
            var Q50;
            Q50=makeQuery(id+"F0.imprint","IMPRINT",FACE,{"disambiguationData":[TD([[makeQuery(id+"F0.imprint","IMPRINT",EDGE,{"derivedFrom":sQuery(id+"F0.wireOp",EDGE,"E25.bottom")}),1.0]])]});
            var Q51;
            Q51=makeQuery(id+"F0.imprint","IMPRINT",FACE,{"disambiguationData":[TD([[makeQuery(id+"F0.imprint","IMPRINT",EDGE,{"derivedFrom":sQuery(id+"F0.wireOp",EDGE,"E32.bottom")}),1.0]])]});
            var Q52;
            Q52=makeQuery(id+"F0.imprint","IMPRINT",FACE,{"disambiguationData":[TD([[makeQuery(id+"F0.imprint","IMPRINT",EDGE,{"derivedFrom":sQuery(id+"F0.wireOp",EDGE,"E40.bottom")}),1.0]])]});
            var Q53;
            Q53=makeQuery(id+"F0.imprint","IMPRINT",FACE,{"disambiguationData":[TD([[makeQuery(id+"F0.imprint","IMPRINT",EDGE,{"derivedFrom":sQuery(id+"F0.wireOp",EDGE,"E52.bottom")}),1.0]])]});
            var Q54;
            Q54=makeQuery(id+"F0.imprint","IMPRINT",FACE,{"disambiguationData":[TD([[makeQuery(id+"F0.imprint","IMPRINT",EDGE,{"derivedFrom":sQuery(id+"F0.wireOp",EDGE,"E55.bottom")}),1.0]])]});
            var Q55;
            Q55=makeQuery(id+"F0.imprint","IMPRINT",FACE,{"disambiguationData":[TD([[makeQuery(id+"F0.imprint","IMPRINT",EDGE,{"derivedFrom":sQuery(id+"F0.wireOp",EDGE,"E64.bottom")}),1.0]])]});
            var Q56;
            Q56=makeQuery(id+"F0.imprint","IMPRINT",FACE,{"disambiguationData":[TD([[makeQuery(id+"F0.imprint","IMPRINT",EDGE,{"derivedFrom":sQuery(id+"F0.wireOp",EDGE,"E65.bottom")}),1.0]])]});
            var Q57;
            Q57=makeQuery(id+"F0.imprint","IMPRINT",FACE,{"disambiguationData":[TD([[makeQuery(id+"F0.imprint","IMPRINT",EDGE,{"derivedFrom":sQuery(id+"F0.wireOp",EDGE,"E54.bottom")}),1.0]])]});
            var Q58;
            Q58=makeQuery(id+"F0.imprint","IMPRINT",FACE,{"disambiguationData":[TD([[makeQuery(id+"F0.imprint","IMPRINT",EDGE,{"derivedFrom":sQuery(id+"F0.wireOp",EDGE,"E53.bottom")}),1.0]])]});
            var Q59;
            Q59=makeQuery(id+"F0.imprint","IMPRINT",FACE,{"disambiguationData":[TD([[makeQuery(id+"F0.imprint","IMPRINT",EDGE,{"derivedFrom":sQuery(id+"F0.wireOp",EDGE,"E91.bottom")}),1.0]])]});
            var Q60;
            Q60=makeQuery(id+"F0.imprint","IMPRINT",FACE,{"disambiguationData":[TD([[makeQuery(id+"F0.imprint","IMPRINT",EDGE,{"derivedFrom":sQuery(id+"F0.wireOp",EDGE,"E33.bottom")}),1.0]])]});
            var Q61;
            Q61=makeQuery(id+"F0.imprint","IMPRINT",FACE,{"disambiguationData":[TD([[makeQuery(id+"F0.imprint","IMPRINT",EDGE,{"derivedFrom":sQuery(id+"F0.wireOp",EDGE,"E26.bottom")}),1.0]])]});
            var Q62;
            Q62=makeQuery(id+"F0.imprint","IMPRINT",FACE,{"disambiguationData":[TD([[makeQuery(id+"F0.imprint","IMPRINT",EDGE,{"derivedFrom":sQuery(id+"F0.wireOp",EDGE,"E19.bottom")}),1.0]])]});
            var Q63;
            Q63=makeQuery(id+"F0.imprint","IMPRINT",FACE,{"disambiguationData":[TD([[makeQuery(id+"F0.imprint","IMPRINT",EDGE,{"derivedFrom":sQuery(id+"F0.wireOp",EDGE,"E8.bottom")}),1.0]])]});
            extrude(context, id + "F2", {"entities" : qUnion([Q0, Q1, Q2, Q3, Q4, Q5, Q6, Q7, Q8, Q9, Q10, Q11, Q12, Q13, Q14, Q15, Q16, Q17, Q18, Q19, Q20, Q21, Q22, Q23, Q24, Q25, Q26, Q27, Q28, Q29, Q30, Q31, Q32, Q33, Q34, Q35, Q36, Q37, Q38, Q39, Q40, Q41, Q42, Q43, Q44, Q45, Q46, Q47, Q48, Q49, Q50, Q51, Q52, Q53, Q54, Q55, Q56, Q57, Q58, Q59, Q60, Q61, Q62, Q63]), "operationType" : NewBodyOperationType.ADD, "depth" : 1.27 * mm});
        }
    });
